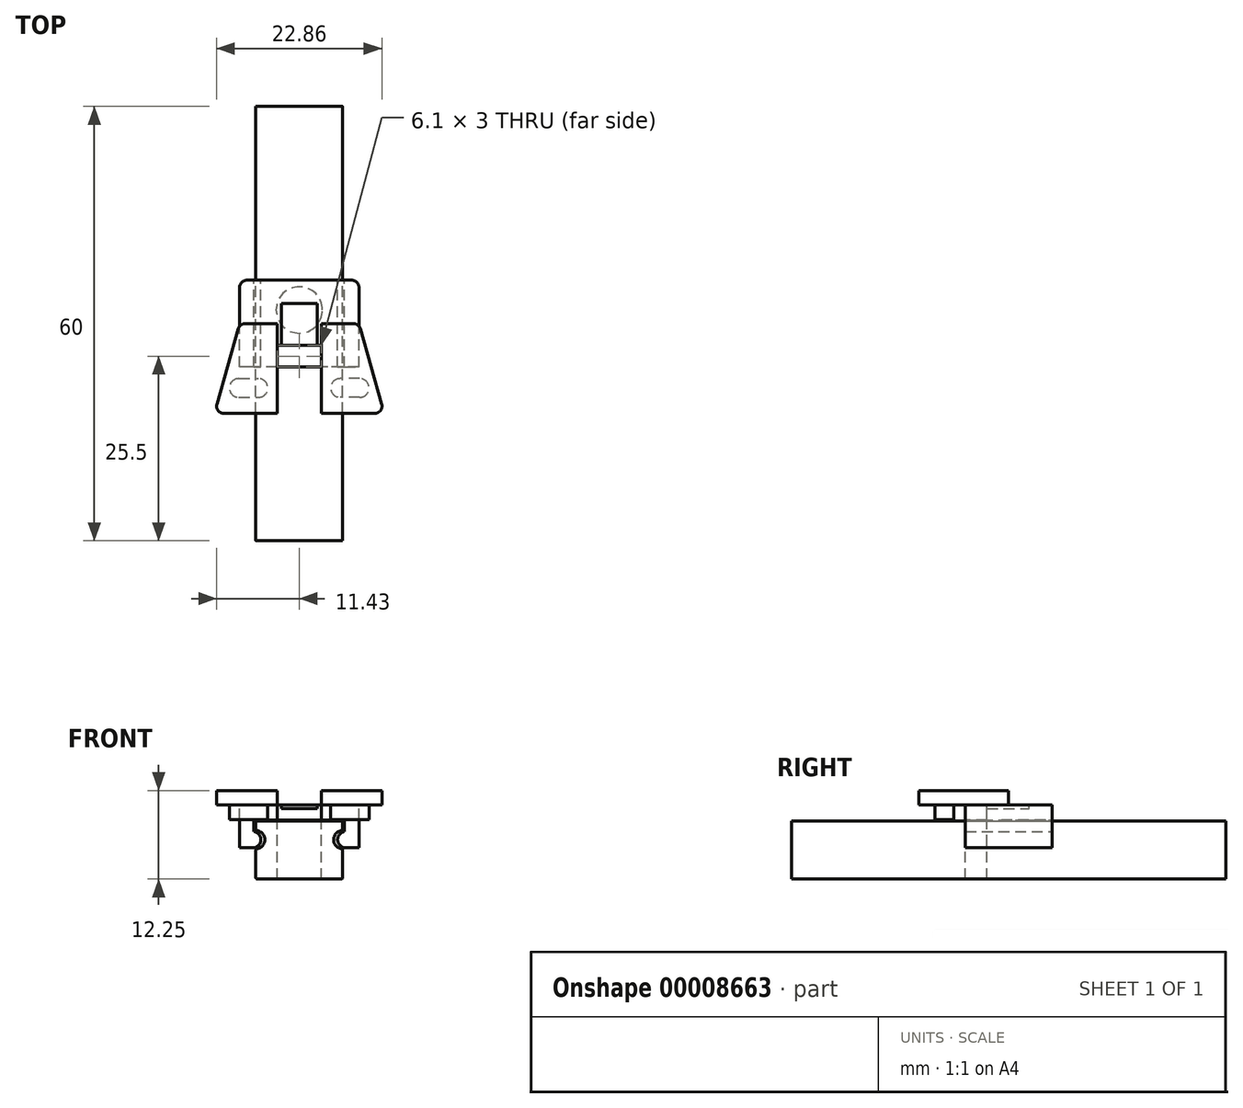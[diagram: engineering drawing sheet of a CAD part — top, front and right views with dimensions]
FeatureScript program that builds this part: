
annotation { "Feature Type Name" : "Feature", "Feature Type Description" : "" }
export const myFeature = defineFeature(function(context is Context, id is Id, definition is map)
    precondition{}
    {
        {
            var Q0;
            Q0=qCreatedBy(makeId("Front.planeOp"),FACE);
            var sketch = newSketch(context, id + "F0", { "sketchPlane" : qUnion([Q0])});
            skLineSegment(sketch, "E0.rect.bottom", {"start": v(6, -4) * mm, "end": v(-6, -4) * mm});
            skLineSegment(sketch, "E0.rect.top", {"start": v(6, 4) * mm, "end": v(-6, 4) * mm});
            skLineSegment(sketch, "E0.rect.left", {"start": v(6, -4) * mm, "end": v(6, 4) * mm});
            skLineSegment(sketch, "E0.rect.right", {"start": v(-6, -4) * mm, "end": v(-6, 4) * mm});
            skPoint(sketch, "E0.rect.middle", {"position": v(0, 0) * mm});
            skSolve(sketch);
        }
        {
            var Q0;
            Q0 = qSketchRegion(id + "F0", true);
            extrude(context, id + "F1", {"entities" : qUnion([Q0]), "endBound" : BoundingType.SYMMETRIC, "depth" : 60 * mm});
        }
        {
            var Q0;
            Q0=makeQuery(id+"F1.opExtrude","CAP_FACE",FACE,{"disambiguationData":[OSD([sQuery(id+"F0.wireOp",EDGE,"E0.rect.bottom"),sQuery(id+"F0.wireOp",EDGE,"E0.rect.top"),sQuery(id+"F0.wireOp",EDGE,"E0.rect.left"),sQuery(id+"F0.wireOp",EDGE,"E0.rect.right")])],"isStart":false});
            var sketch = newSketch(context, id + "F2", { "sketchPlane" : qUnion([Q0])});
            skCircle(sketch, "E1", {"center": v(-6, 1.45) * mm, "radius": 1.25 * mm});
            skCircle(sketch, "E2", {"center": v(6, 1.45) * mm, "radius": 1.25 * mm});
            skSolve(sketch);
        }
        {
            var Q0;
            Q0 = qSketchRegion(id + "F2", true);
            extrude(context, id + "F3", {"entities" : qUnion([Q0]), "operationType" : NewBodyOperationType.REMOVE, "oppositeDirection" : true, "depth" : 60 * mm});
        }
        {
            var Q0;
            Q0=makeQuery(id+"F1.opExtrude","SWEPT_EDGE",EDGE,{"disambiguationData":[OSD([sQuery(id+"F0.wireOp",EDGE,"E0.rect.top"),sQuery(id+"F0.wireOp",EDGE,"E0.rect.left")])]});
            var Q1;
            Q1=makeQuery(id+"F3.boolean.opBoolean","INTERSECT",EDGE,{"disambiguationData":[OD(1.0)],"derivedFrom":[makeQuery(id+"F1.opExtrude","SWEPT_FACE",FACE,{"disambiguationData":[OSD([sQuery(id+"F0.wireOp",EDGE,"E0.rect.left")])]}),makeQuery(id+"F3.opExtrude","SWEPT_FACE",FACE,{"disambiguationData":[OSD([sQuery(id+"F2.wireOp",EDGE,"E2")])]})]});
            var Q2;
            Q2=makeQuery(id+"F3.boolean.opBoolean","INTERSECT",EDGE,{"disambiguationData":[OD(0.0)],"derivedFrom":[makeQuery(id+"F1.opExtrude","SWEPT_FACE",FACE,{"disambiguationData":[OSD([sQuery(id+"F0.wireOp",EDGE,"E0.rect.left")])]}),makeQuery(id+"F3.opExtrude","SWEPT_FACE",FACE,{"disambiguationData":[OSD([sQuery(id+"F2.wireOp",EDGE,"E2")])]})]});
            var Q3;
            Q3=makeQuery(id+"F1.opExtrude","SWEPT_EDGE",EDGE,{"disambiguationData":[OSD([sQuery(id+"F0.wireOp",EDGE,"E0.rect.bottom"),sQuery(id+"F0.wireOp",EDGE,"E0.rect.left")])]});
            var Q4;
            Q4=makeQuery(id+"F1.opExtrude","SWEPT_EDGE",EDGE,{"disambiguationData":[OSD([sQuery(id+"F0.wireOp",EDGE,"E0.rect.top"),sQuery(id+"F0.wireOp",EDGE,"E0.rect.right")])]});
            var Q5;
            Q5=makeQuery(id+"F3.boolean.opBoolean","INTERSECT",EDGE,{"disambiguationData":[OD(1.0)],"derivedFrom":[makeQuery(id+"F1.opExtrude","SWEPT_FACE",FACE,{"disambiguationData":[OSD([sQuery(id+"F0.wireOp",EDGE,"E0.rect.right")])]}),makeQuery(id+"F3.opExtrude","SWEPT_FACE",FACE,{"disambiguationData":[OSD([sQuery(id+"F2.wireOp",EDGE,"E1")])]})]});
            var Q6;
            Q6=makeQuery(id+"F3.boolean.opBoolean","INTERSECT",EDGE,{"disambiguationData":[OD(0.0)],"derivedFrom":[makeQuery(id+"F1.opExtrude","SWEPT_FACE",FACE,{"disambiguationData":[OSD([sQuery(id+"F0.wireOp",EDGE,"E0.rect.right")])]}),makeQuery(id+"F3.opExtrude","SWEPT_FACE",FACE,{"disambiguationData":[OSD([sQuery(id+"F2.wireOp",EDGE,"E1")])]})]});
            var Q7;
            Q7=makeQuery(id+"F1.opExtrude","SWEPT_EDGE",EDGE,{"disambiguationData":[OSD([sQuery(id+"F0.wireOp",EDGE,"E0.rect.bottom"),sQuery(id+"F0.wireOp",EDGE,"E0.rect.right")])]});
            fillet(context, id + "F4", {"entities" : qUnion([Q0, Q1, Q2, Q3, Q4, Q5, Q6, Q7]), "radius" : .2 * mm, "tangentPropagation" : true, "allowEdgeOverflow" : false});
        }
        {
            var Q0;
            Q0=qCreatedBy(makeId("Front.planeOp"),FACE);
            var sketch = newSketch(context, id + "F5", { "sketchPlane" : qUnion([Q0])});
            skLineSegment(sketch, "E3.rect.bottom", {"start": v(6.25, 4.15) * mm, "end": v(-6.25, 4.15) * mm});
            skPoint(sketch, "E3.rect.middle", {"position": v(0, 0) * mm});
            skPoint(sketch, "E3.rect.top.end.orphan", {"position": v(-6.25, -4.15) * mm});
            skPoint(sketch, "E4.orphan", {"position": v(6.25, -4.15) * mm});
            skLineSegment(sketch, "E5.rect.top", {"start": v(8.25, 6.25) * mm, "end": v(-8.25, 6.25) * mm});
            skLineSegment(sketch, "E5.rect.left", {"start": v(8.25, 0.32) * mm, "end": v(8.25, 6.25) * mm});
            skLineSegment(sketch, "E5.rect.right", {"start": v(-8.25, 0.32) * mm, "end": v(-8.25, 6.25) * mm});
            skLineSegment(sketch, "E6", {"start": v(-6.25, 0.32) * mm, "end": v(-8.25, 0.32) * mm});
            skLineSegment(sketch, "E7", {"start": v(6.25, 0.32) * mm, "end": v(8.25, 0.32) * mm});
            skPoint(sketch, "E5.rect.bottom.end.orphan", {"position": v(-8.25, -6.25) * mm});
            skPoint(sketch, "E8.orphan", {"position": v(8.25, -6.25) * mm});
            skLineSegment(sketch, "E9", {"start": v(-6.25, 4.15) * mm, "end": v(-6.25, 2.58) * mm});
            skArc(sketch, "E10", {"start": v(-6.64, 0.32) * mm, "mid": v(-5.32, 1.25) * mm, "end": v(-6.25, 2.58) * mm});
            skArc(sketch, "E11", {"start": v(6.25, 2.58) * mm, "mid": v(5.32, 1.25) * mm, "end": v(6.64, 0.32) * mm});
            skLineSegment(sketch, "E12", {"start": v(6.25, 4.15) * mm, "end": v(6.25, 2.58) * mm});
            skSolve(sketch);
        }
        {
            var Q0;
            Q0=makeQuery(id+"F5.imprint","IMPRINT",FACE,{"disambiguationData":[TD([[makeQuery(id+"F5.imprint","IMPRINT",EDGE,{"derivedFrom":sQuery(id+"F5.wireOp",EDGE,"E3.rect.bottom")}),-1.0]])]});
            extrude(context, id + "F6", {"entities" : qUnion([Q0]), "endBound" : BoundingType.SYMMETRIC, "depth" : 12 * mm});
        }
        {
            var Q0;
            Q0=makeQuery(id+"F6.opExtrude","SWEPT_FACE",FACE,{"disambiguationData":[OSD([sQuery(id+"F5.wireOp",EDGE,"E5.rect.top")])]});
            var sketch = newSketch(context, id + "F7", { "sketchPlane" : qUnion([Q0])});
            skLineSegment(sketch, "E13.bottom", {"start": v(-3.05, -6) * mm, "end": v(3.05, -6) * mm});
            skLineSegment(sketch, "E13.top", {"start": v(-3.05, -3) * mm, "end": v(3.05, -3) * mm});
            skLineSegment(sketch, "E13.left", {"start": v(-3.05, -6) * mm, "end": v(-3.05, -3) * mm});
            skLineSegment(sketch, "E13.right", {"start": v(3.05, -6) * mm, "end": v(3.05, -3) * mm});
            skLineSegment(sketch, "E14", {"start": v(0, 0) * mm, "end": v(0, -3) * mm});
            skSolve(sketch);
        }
        {
            var Q0;
            Q0=makeQuery(id+"F7.imprint","IMPRINT",FACE,{"disambiguationData":[TD([[makeQuery(id+"F7.imprint","IMPRINT",EDGE,{"derivedFrom":sQuery(id+"F7.wireOp",EDGE,"E13.bottom")}),-1.0]])]});
            extrude(context, id + "F8", {"entities" : qUnion([Q0]), "operationType" : NewBodyOperationType.REMOVE, "endBound" : BoundingType.THROUGH_ALL, "oppositeDirection" : true, "depth" : 25 * mm});
        }
        {
            var Q0;
            Q0=makeQuery(id+"F6.opExtrude","SWEPT_FACE",FACE,{"disambiguationData":[OSD([sQuery(id+"F5.wireOp",EDGE,"E5.rect.top")])]});
            var sketch = newSketch(context, id + "F9", { "sketchPlane" : qUnion([Q0])});
            skLineSegment(sketch, "E15.bottom", {"start": v(-2.5, -3) * mm, "end": v(2.5, -3) * mm});
            skLineSegment(sketch, "E15.top", {"start": v(-2.5, 2.8) * mm, "end": v(2.5, 2.8) * mm});
            skLineSegment(sketch, "E15.left", {"start": v(-2.5, -3) * mm, "end": v(-2.5, 2.8) * mm});
            skLineSegment(sketch, "E15.right", {"start": v(2.5, -3) * mm, "end": v(2.5, 2.8) * mm});
            skLineSegment(sketch, "E16", {"start": v(0, 0) * mm, "end": v(0, 2.8) * mm});
            skSolve(sketch);
        }
        {
            var Q0;
            Q0=makeQuery(id+"F9.imprint","IMPRINT",FACE,{"disambiguationData":[TD([[makeQuery(id+"F9.imprint","IMPRINT",EDGE,{"derivedFrom":sQuery(id+"F9.wireOp",EDGE,"E15.bottom")}),1.0]])]});
            extrude(context, id + "F10", {"entities" : qUnion([Q0]), "operationType" : NewBodyOperationType.REMOVE, "oppositeDirection" : true, "depth" : .5 * mm});
        }
        {
            var Q0;
            Q0=makeQuery(id+"F6.opExtrude","SWEPT_FACE",FACE,{"disambiguationData":[OSD([sQuery(id+"F5.wireOp",EDGE,"E3.rect.bottom")])]});
            var sketch = newSketch(context, id + "F11", { "sketchPlane" : qUnion([Q0])});
            skCircle(sketch, "E17", {"center": v(0, -1.88) * mm, "radius": 3.2 * mm});
            skSolve(sketch);
        }
        {
            var Q0;
            Q0=makeQuery(id+"F11.imprint","IMPRINT",FACE,{"disambiguationData":[TD([[makeQuery(id+"F11.imprint","IMPRINT",EDGE,{"derivedFrom":sQuery(id+"F11.wireOp",EDGE,"E17")}),1.0]])]});
            extrude(context, id + "F12", {"entities" : qUnion([Q0]), "operationType" : NewBodyOperationType.ADD, "depth" : 2 * mm});
        }
        {
            var Q0;
            Q0=makeQuery(id+"F6.opExtrude","SWEPT_FACE",FACE,{"disambiguationData":[OSD([sQuery(id+"F5.wireOp",EDGE,"E5.rect.top")])]});
            var sketch = newSketch(context, id + "F13", { "sketchPlane" : qUnion([Q0])});
            skLineSegment(sketch, "E18.bottom", {"start": v(-3.05, 0) * mm, "end": v(-8.25, 0) * mm});
            skLineSegment(sketch, "E18.top", {"start": v(-3.05, -12.4) * mm, "end": v(-11.75, -12.4) * mm});
            skLineSegment(sketch, "E18.left", {"start": v(-3.05, 0) * mm, "end": v(-3.05, -12.4) * mm});
            skLineSegment(sketch, "E19", {"start": v(0, -3) * mm, "end": v(0, -12.4) * mm, "construction": true});
            skLineSegment(sketch, "E20", {"start": v(-11.75, -12.4) * mm, "end": v(-8.25, 0) * mm});
            skLineSegment(sketch, "E21.0.MirrorCS", {"start": v(3.05, 0) * mm, "end": v(3.05, -12.4) * mm});
            skLineSegment(sketch, "E22.0.MirrorCS", {"start": v(3.05, 0) * mm, "end": v(8.25, 0) * mm});
            skLineSegment(sketch, "E23.0.MirrorCS", {"start": v(11.75, -12.4) * mm, "end": v(8.25, 0) * mm});
            skLineSegment(sketch, "E24.0.MirrorCS", {"start": v(3.05, -12.4) * mm, "end": v(11.75, -12.4) * mm});
            skSolve(sketch);
        }
        {
            var Q0;
            Q0 = qSketchRegion(id + "F13", true);
            extrude(context, id + "F14", {"entities" : qUnion([Q0]), "operationType" : NewBodyOperationType.ADD, "depth" : 2 * mm});
        }
        {
            var Q0;
            Q0=makeQuery(id+"F14.opExtrude","CAP_FACE",FACE,{"disambiguationData":[OSD([sQuery(id+"F13.wireOp",EDGE,"E18.bottom"),sQuery(id+"F13.wireOp",EDGE,"E18.top"),sQuery(id+"F13.wireOp",EDGE,"E18.left"),sQuery(id+"F13.wireOp",EDGE,"E20")])],"isStart":true});
            var sketch = newSketch(context, id + "F15", { "sketchPlane" : qUnion([Q0])});
            skArc(sketch, "E25", {"start": v(-8.35, 10.2) * mm, "mid": v(-9.65, 8.9) * mm, "end": v(-8.35, 7.6) * mm});
            skArc(sketch, "E26", {"start": v(-5.65, 7.6) * mm, "mid": v(-4.35, 8.9) * mm, "end": v(-5.65, 10.2) * mm});
            skLineSegment(sketch, "E27", {"start": v(-8.35, 7.6) * mm, "end": v(-5.65, 7.6) * mm});
            skLineSegment(sketch, "E28", {"start": v(-8.35, 10.2) * mm, "end": v(-5.65, 10.2) * mm});
            skLineSegment(sketch, "E29", {"start": v(0, -0.65) * mm, "end": v(0, 8.28) * mm});
            skArc(sketch, "E30.0.MirrorC", {"start": v(8.35, 10.2) * mm, "mid": v(9.65, 8.9) * mm, "end": v(8.35, 7.6) * mm});
            skLineSegment(sketch, "E31.0.MirrorCS", {"start": v(8.35, 10.2) * mm, "end": v(5.65, 10.2) * mm});
            skArc(sketch, "E32.0.MirrorC", {"start": v(5.65, 7.6) * mm, "mid": v(4.35, 8.9) * mm, "end": v(5.65, 10.2) * mm});
            skLineSegment(sketch, "E33.0.MirrorCS", {"start": v(8.35, 7.6) * mm, "end": v(5.65, 7.6) * mm});
            skSolve(sketch);
        }
        {
            var Q0;
            Q0 = qSketchRegion(id + "F15", true);
            extrude(context, id + "F16", {"entities" : qUnion([Q0]), "operationType" : NewBodyOperationType.ADD, "depth" : 2 * mm});
        }
        {
            var Q0;
            Q0=makeQuery(id+"F14.opExtrude","SWEPT_EDGE",EDGE,{"disambiguationData":[OSD([sQuery(id+"F13.wireOp",EDGE,"E18.top"),sQuery(id+"F13.wireOp",EDGE,"E20")])]});
            var Q1;
            Q1=makeQuery(id+"F14.opExtrude","SWEPT_EDGE",EDGE,{"disambiguationData":[OSD([sQuery(id+"F5.wireOp",EDGE,"E5.rect.top"),sQuery(id+"F5.wireOp",EDGE,"E5.rect.right"),sQuery(id+"F13.wireOp",EDGE,"E18.bottom"),sQuery(id+"F13.wireOp",EDGE,"E20")])]});
            fillet(context, id + "F17", {"entities" : qUnion([Q0, Q1]), "radius" : 1 * mm, "tangentPropagation" : true, "allowEdgeOverflow" : false});
        }
        {
            var Q0;
            Q0=makeQuery(id+"F14.opExtrude","SWEPT_EDGE",EDGE,{"disambiguationData":[OSD([sQuery(id+"F13.wireOp",EDGE,"E23.0.MirrorCS"),sQuery(id+"F13.wireOp",EDGE,"E24.0.MirrorCS")])]});
            var Q1;
            Q1=makeQuery(id+"F14.opExtrude","SWEPT_EDGE",EDGE,{"disambiguationData":[OSD([sQuery(id+"F5.wireOp",EDGE,"E5.rect.top"),sQuery(id+"F5.wireOp",EDGE,"E5.rect.left"),sQuery(id+"F13.wireOp",EDGE,"E22.0.MirrorCS"),sQuery(id+"F13.wireOp",EDGE,"E23.0.MirrorCS")])]});
            fillet(context, id + "F18", {"entities" : qUnion([Q0, Q1]), "radius" : 1 * mm, "tangentPropagation" : true, "allowEdgeOverflow" : false});
        }
        {
            var Q0;
            Q0=makeQuery(id+"F6.opExtrude","CAP_EDGE",EDGE,{"disambiguationData":[OSD([sQuery(id+"F5.wireOp",EDGE,"E5.rect.right")])],"isStart":true});
            var Q1;
            Q1=makeQuery(id+"F6.opExtrude","CAP_EDGE",EDGE,{"disambiguationData":[OSD([sQuery(id+"F5.wireOp",EDGE,"E5.rect.left")])],"isStart":true});
            fillet(context, id + "F19", {"entities" : qUnion([Q0, Q1]), "radius" : 1 * mm, "tangentPropagation" : true, "allowEdgeOverflow" : false});
        }
    });
